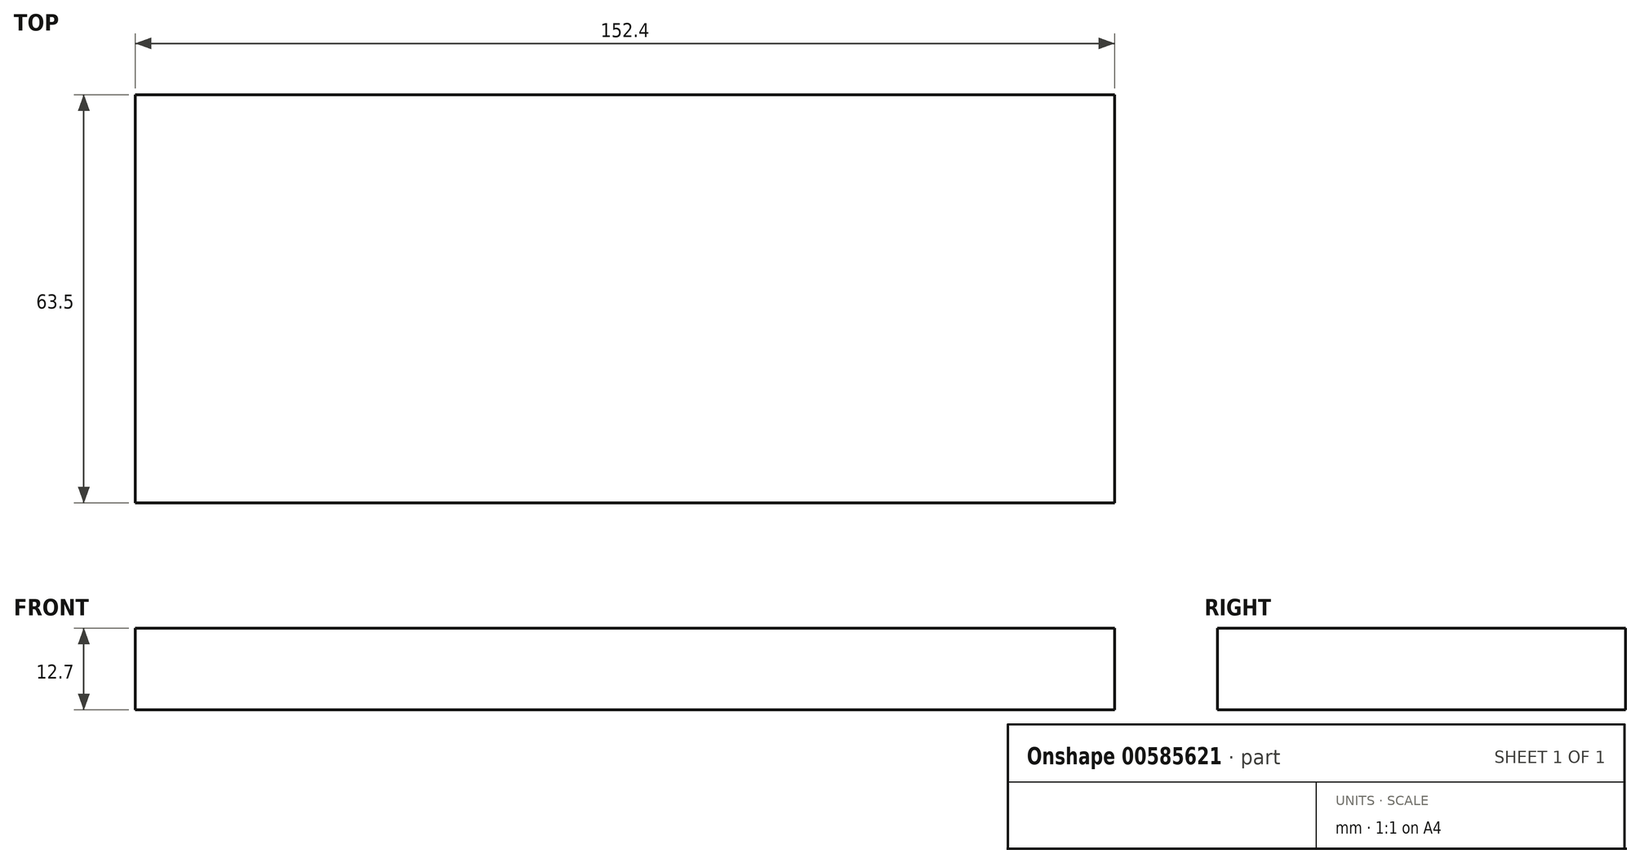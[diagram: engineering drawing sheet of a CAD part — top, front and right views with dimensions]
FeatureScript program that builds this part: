
annotation { "Feature Type Name" : "Feature", "Feature Type Description" : "" }
export const myFeature = defineFeature(function(context is Context, id is Id, definition is map)
    precondition{}
    {
        {
            var Q0;
            Q0=qCreatedBy(makeId("Top.planeOp"),FACE);
            var sketch = newSketch(context, id + "F0", { "sketchPlane" : qUnion([Q0])});
            skLineSegment(sketch, "E0.bottom", {"start": v(-76.2, -31.75) * mm, "end": v(76.2, -31.75) * mm});
            skLineSegment(sketch, "E0.top", {"start": v(-76.2, 31.75) * mm, "end": v(76.2, 31.75) * mm});
            skLineSegment(sketch, "E0.left", {"start": v(-76.2, -31.75) * mm, "end": v(-76.2, 31.75) * mm});
            skLineSegment(sketch, "E0.right", {"start": v(76.2, -31.75) * mm, "end": v(76.2, 31.75) * mm});
            skPoint(sketch, "E0.middle", {"position": v(0, 0) * mm});
            skSolve(sketch);
        }
        {
            var Q0;
            Q0=makeQuery(id+"F0.imprint","IMPRINT",FACE,{"disambiguationData":[TD([[makeQuery(id+"F0.imprint","IMPRINT",EDGE,{"derivedFrom":sQuery(id+"F0.wireOp",EDGE,"E0.bottom")}),1.0]])]});
            extrude(context, id + "F1", {"entities" : qUnion([Q0]), "depth" : 12.7 * mm, "offsetDistance" : 25.4 * mm});
        }
    });
